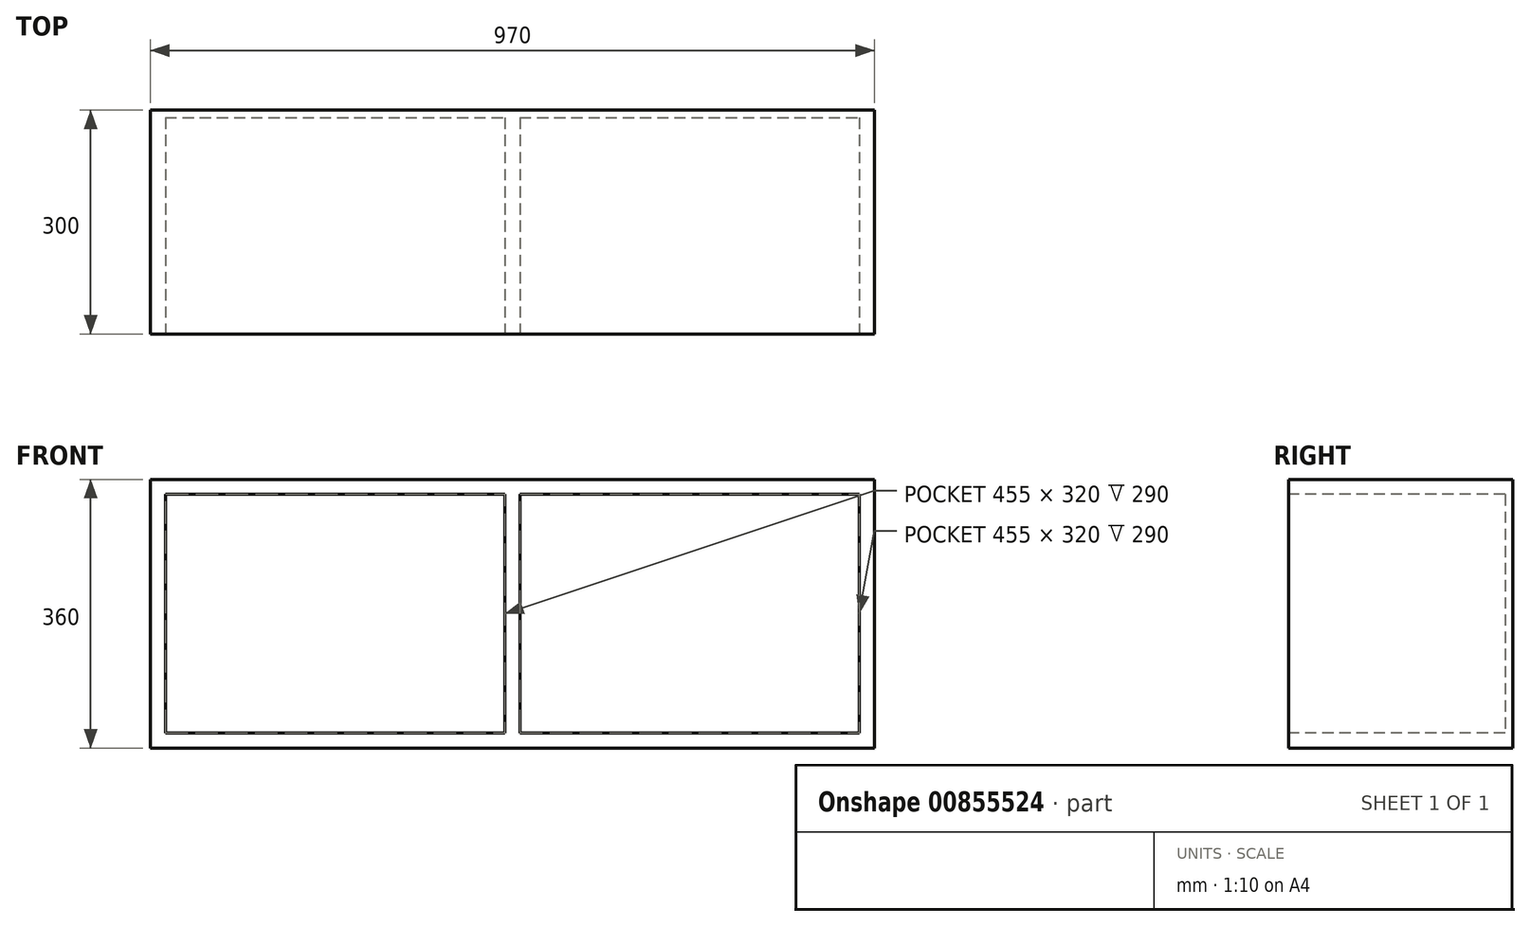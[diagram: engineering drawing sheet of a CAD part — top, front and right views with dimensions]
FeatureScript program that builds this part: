
annotation { "Feature Type Name" : "Feature", "Feature Type Description" : "" }
export const myFeature = defineFeature(function(context is Context, id is Id, definition is map)
    precondition{}
    {
        {
            var Q0;
            Q0=qCreatedBy(makeId("Top.planeOp"),FACE);
            var sketch = newSketch(context, id + "F0", { "sketchPlane" : qUnion([Q0])});
            skLineSegment(sketch, "E0.bottom", {"start": v(-239.35, 58.5) * mm, "end": v(730.65, 58.5) * mm});
            skLineSegment(sketch, "E0.top", {"start": v(-239.35, -241.5) * mm, "end": v(730.65, -241.5) * mm});
            skLineSegment(sketch, "E0.left", {"start": v(-239.35, 58.5) * mm, "end": v(-239.35, -241.5) * mm});
            skLineSegment(sketch, "E0.right", {"start": v(730.65, 58.5) * mm, "end": v(730.65, -241.5) * mm});
            skSolve(sketch);
        }
        {
            var Q0;
            Q0=makeQuery(id+"F0.imprint","IMPRINT",FACE,{"disambiguationData":[TD([[makeQuery(id+"F0.imprint","IMPRINT",EDGE,{"derivedFrom":sQuery(id+"F0.wireOp",EDGE,"E0.bottom")}),-1.0]])]});
            extrude(context, id + "F1", {"entities" : qUnion([Q0]), "depth" : 360 * mm, "offsetDistance" : 25.4 * mm});
        }
        {
            var Q0;
            Q0=makeQuery(id+"F1.opExtrude","SWEPT_FACE",FACE,{"disambiguationData":[OSD([sQuery(id+"F0.wireOp",EDGE,"E0.top")])]});
            var sketch = newSketch(context, id + "F2", { "sketchPlane" : qUnion([Q0])});
            skLineSegment(sketch, "E1.bottom", {"start": v(-219.35, 340) * mm, "end": v(235.65, 340) * mm});
            skLineSegment(sketch, "E1.top", {"start": v(-219.35, 20) * mm, "end": v(235.65, 20) * mm});
            skLineSegment(sketch, "E1.left", {"start": v(-219.35, 340) * mm, "end": v(-219.35, 20) * mm});
            skLineSegment(sketch, "E1.right", {"start": v(235.65, 340) * mm, "end": v(235.65, 20) * mm});
            skSolve(sketch);
        }
        {
            var Q0;
            Q0=makeQuery(id+"F2.imprint","IMPRINT",FACE,{"disambiguationData":[TD([[makeQuery(id+"F2.imprint","IMPRINT",EDGE,{"derivedFrom":sQuery(id+"F2.wireOp",EDGE,"E1.bottom")}),-1.0]])]});
            extrude(context, id + "F3", {"entities" : qUnion([Q0]), "operationType" : NewBodyOperationType.REMOVE, "oppositeDirection" : true, "depth" : 290 * mm, "offsetDistance" : 25.4 * mm});
        }
        {
            var Q0;
            Q0=makeQuery(id+"F1.opExtrude","SWEPT_FACE",FACE,{"disambiguationData":[OSD([sQuery(id+"F0.wireOp",EDGE,"E0.top")])]});
            var sketch = newSketch(context, id + "F4", { "sketchPlane" : qUnion([Q0])});
            skLineSegment(sketch, "E2.bottom", {"start": v(255.65, 340) * mm, "end": v(710.65, 340) * mm});
            skLineSegment(sketch, "E2.top", {"start": v(255.65, 20) * mm, "end": v(710.65, 20) * mm});
            skLineSegment(sketch, "E2.left", {"start": v(255.65, 340) * mm, "end": v(255.65, 20) * mm});
            skLineSegment(sketch, "E2.right", {"start": v(710.65, 340) * mm, "end": v(710.65, 20) * mm});
            skSolve(sketch);
        }
        {
            var Q0;
            Q0 = qSketchRegion(id + "F4", true);
            extrude(context, id + "F5", {"entities" : qUnion([Q0]), "operationType" : NewBodyOperationType.REMOVE, "oppositeDirection" : true, "depth" : 290 * mm, "offsetDistance" : 25.4 * mm});
        }
    });
